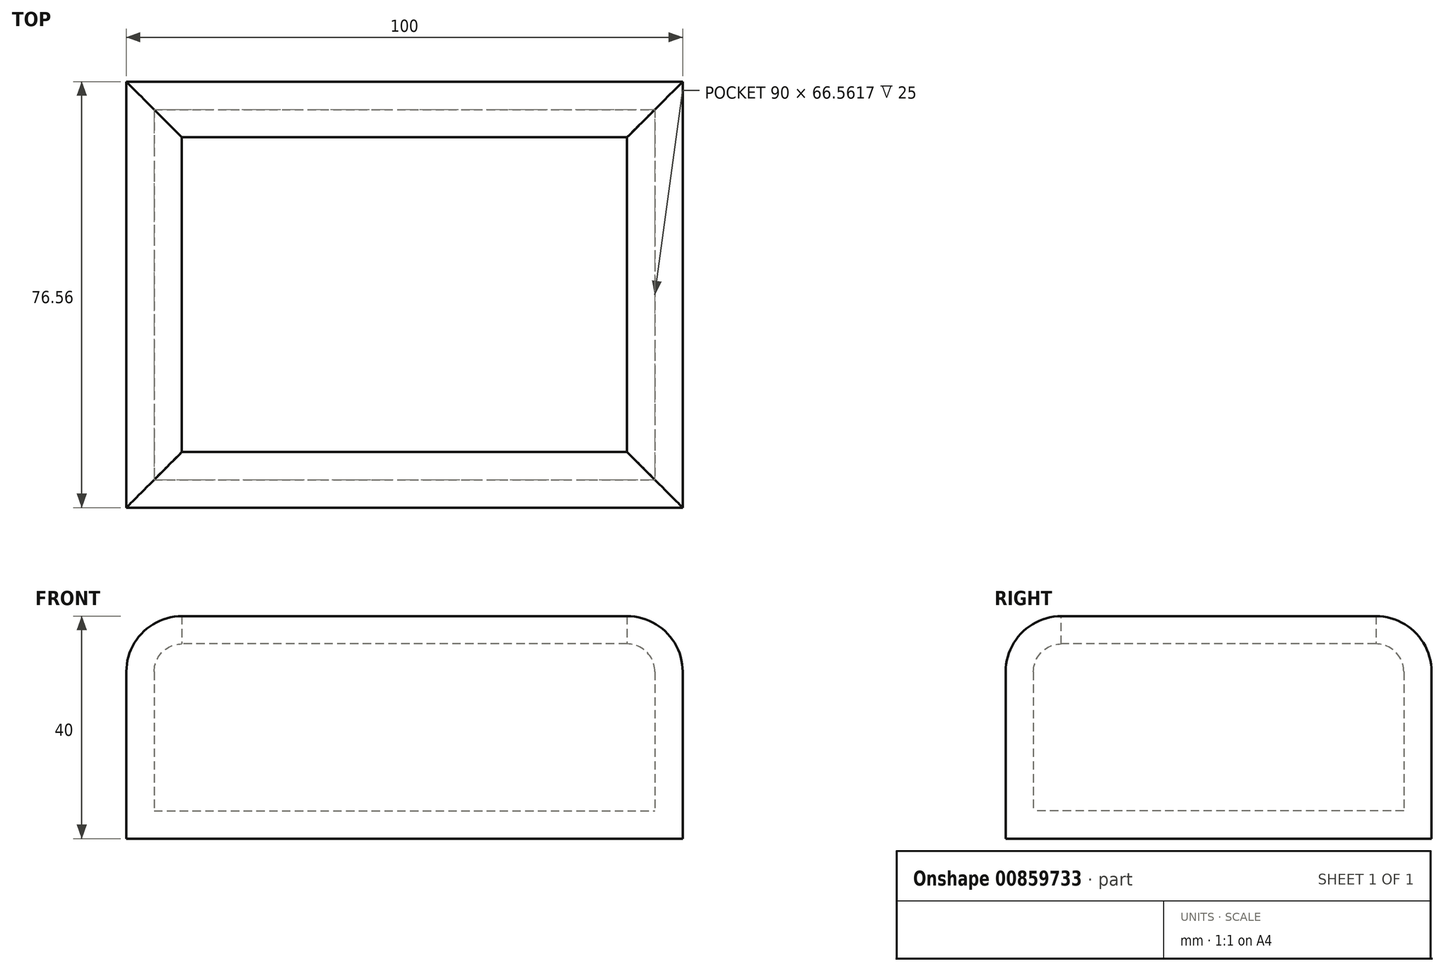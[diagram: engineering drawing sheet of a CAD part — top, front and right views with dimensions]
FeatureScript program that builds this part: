
annotation { "Feature Type Name" : "Feature", "Feature Type Description" : "" }
export const myFeature = defineFeature(function(context is Context, id is Id, definition is map)
    precondition{}
    {
        {
            var Q0;
            Q0=qCreatedBy(makeId("Top.planeOp"),FACE);
            var sketch = newSketch(context, id + "F0", { "sketchPlane" : qUnion([Q0])});
            skLineSegment(sketch, "E0.bottom", {"start": v(-191.03, 0) * mm, "end": v(-91.03, 0) * mm});
            skLineSegment(sketch, "E0.top", {"start": v(-191.03, -76.56) * mm, "end": v(-91.03, -76.56) * mm});
            skLineSegment(sketch, "E0.left", {"start": v(-191.03, 0) * mm, "end": v(-191.03, -76.56) * mm});
            skLineSegment(sketch, "E0.right", {"start": v(-91.03, 0) * mm, "end": v(-91.03, -76.56) * mm});
            skSolve(sketch);
        }
        {
            var Q0;
            Q0 = qSketchRegion(id + "F0", true);
            extrude(context, id + "F1", {"entities" : qUnion([Q0]), "depth" : 40 * mm, "offsetDistance" : 25 * mm});
        }
        {
            var Q0;
            Q0=makeQuery(id+"F1.opExtrude","CAP_EDGE",EDGE,{"disambiguationData":[OSD([sQuery(id+"F0.wireOp",EDGE,"E0.top")])],"isStart":false});
            var Q1;
            Q1=makeQuery(id+"F1.opExtrude","CAP_EDGE",EDGE,{"disambiguationData":[OSD([sQuery(id+"F0.wireOp",EDGE,"E0.right")])],"isStart":false});
            var Q2;
            Q2=makeQuery(id+"F1.opExtrude","CAP_EDGE",EDGE,{"disambiguationData":[OSD([sQuery(id+"F0.wireOp",EDGE,"E0.bottom")])],"isStart":false});
            var Q3;
            Q3=makeQuery(id+"F1.opExtrude","CAP_EDGE",EDGE,{"disambiguationData":[OSD([sQuery(id+"F0.wireOp",EDGE,"E0.left")])],"isStart":false});
            fillet(context, id + "F2", {"entities" : qUnion([Q0, Q1, Q2, Q3]), "radius" : 10 * mm, "tangentPropagation" : true, "allowEdgeOverflow" : false});
        }
        {
            var Q0;
            Q0=makeQuery(id+"F1.opExtrude","CAP_FACE",FACE,{"disambiguationData":[OSD([sQuery(id+"F0.wireOp",EDGE,"E0.bottom"),sQuery(id+"F0.wireOp",EDGE,"E0.top"),sQuery(id+"F0.wireOp",EDGE,"E0.left"),sQuery(id+"F0.wireOp",EDGE,"E0.right")])],"isStart":false});
            shell(context, id + "F3", {"entities" : qUnion([Q0]), "thickness" : 5 * mm});
        }
    });
